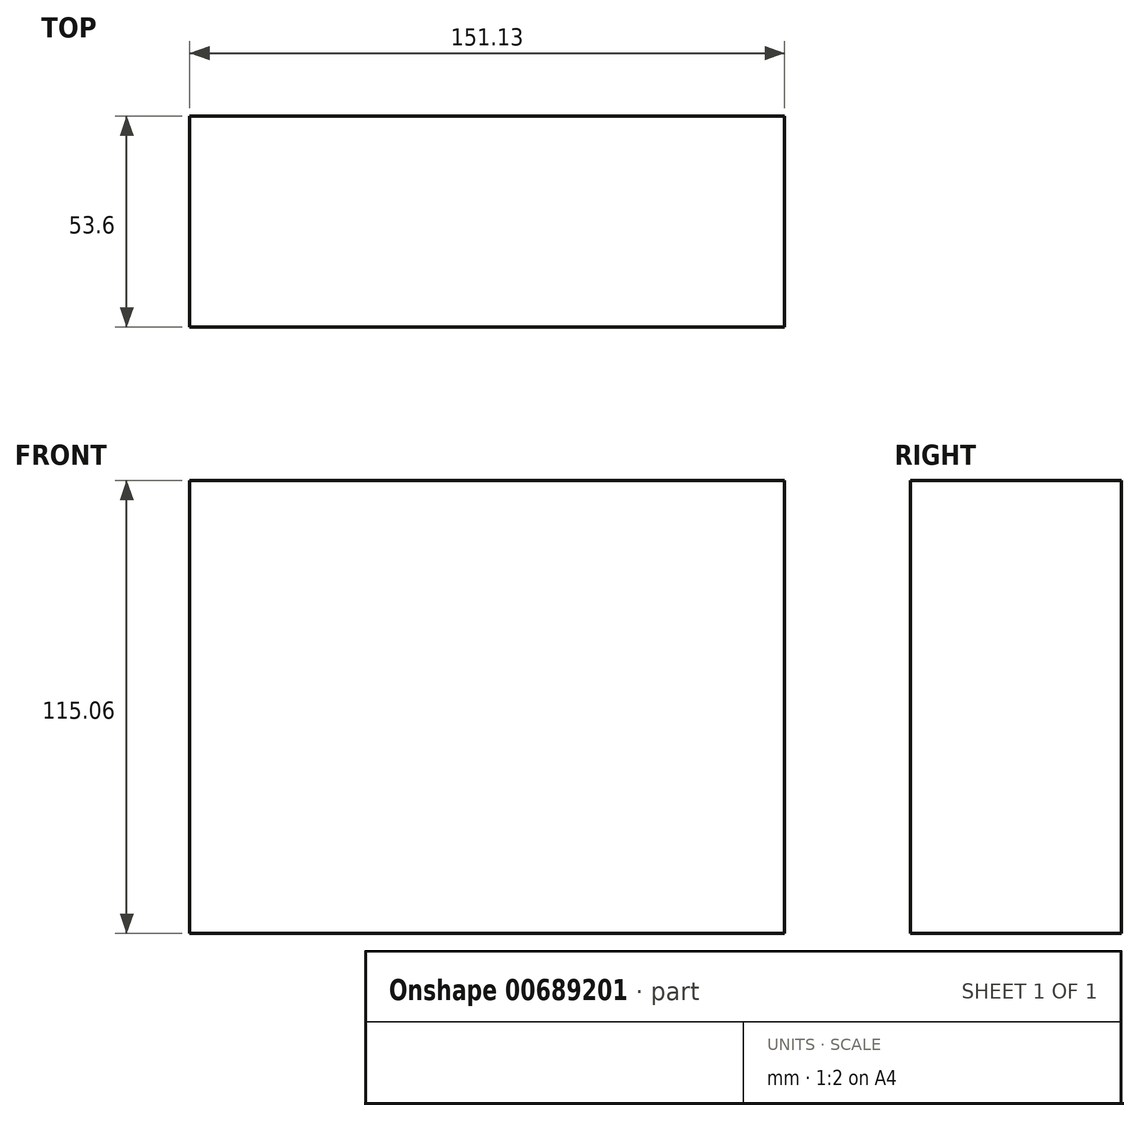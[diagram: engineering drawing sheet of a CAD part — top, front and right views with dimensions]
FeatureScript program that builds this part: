
annotation { "Feature Type Name" : "Feature", "Feature Type Description" : "" }
export const myFeature = defineFeature(function(context is Context, id is Id, definition is map)
    precondition{}
    {
        {
            var Q0;
            Q0=qCreatedBy(makeId("Top.planeOp"),FACE);
            var sketch = newSketch(context, id + "F0", { "sketchPlane" : qUnion([Q0])});
            skLineSegment(sketch, "E0.bottom", {"start": v(-100.32, 53.3) * mm, "end": v(50.8, 53.3) * mm});
            skLineSegment(sketch, "E0.top", {"start": v(-100.32, -0.3) * mm, "end": v(50.8, -0.3) * mm});
            skLineSegment(sketch, "E0.left", {"start": v(-100.32, 53.3) * mm, "end": v(-100.32, -0.3) * mm});
            skLineSegment(sketch, "E0.right", {"start": v(50.8, 53.3) * mm, "end": v(50.8, -0.3) * mm});
            skPoint(sketch, "E0.middle", {"position": v(-24.76, 26.5) * mm});
            skSolve(sketch);
        }
        {
            var Q0;
            Q0=makeQuery(id+"F0.imprint","IMPRINT",FACE,{"disambiguationData":[TD([[makeQuery(id+"F0.imprint","IMPRINT",EDGE,{"derivedFrom":sQuery(id+"F0.wireOp",EDGE,"E0.bottom")}),-1.0]])]});
            extrude(context, id + "F1", {"entities" : qUnion([Q0]), "depth" : 115.06 * mm, "offsetDistance" : 25.4 * mm});
        }
    });
